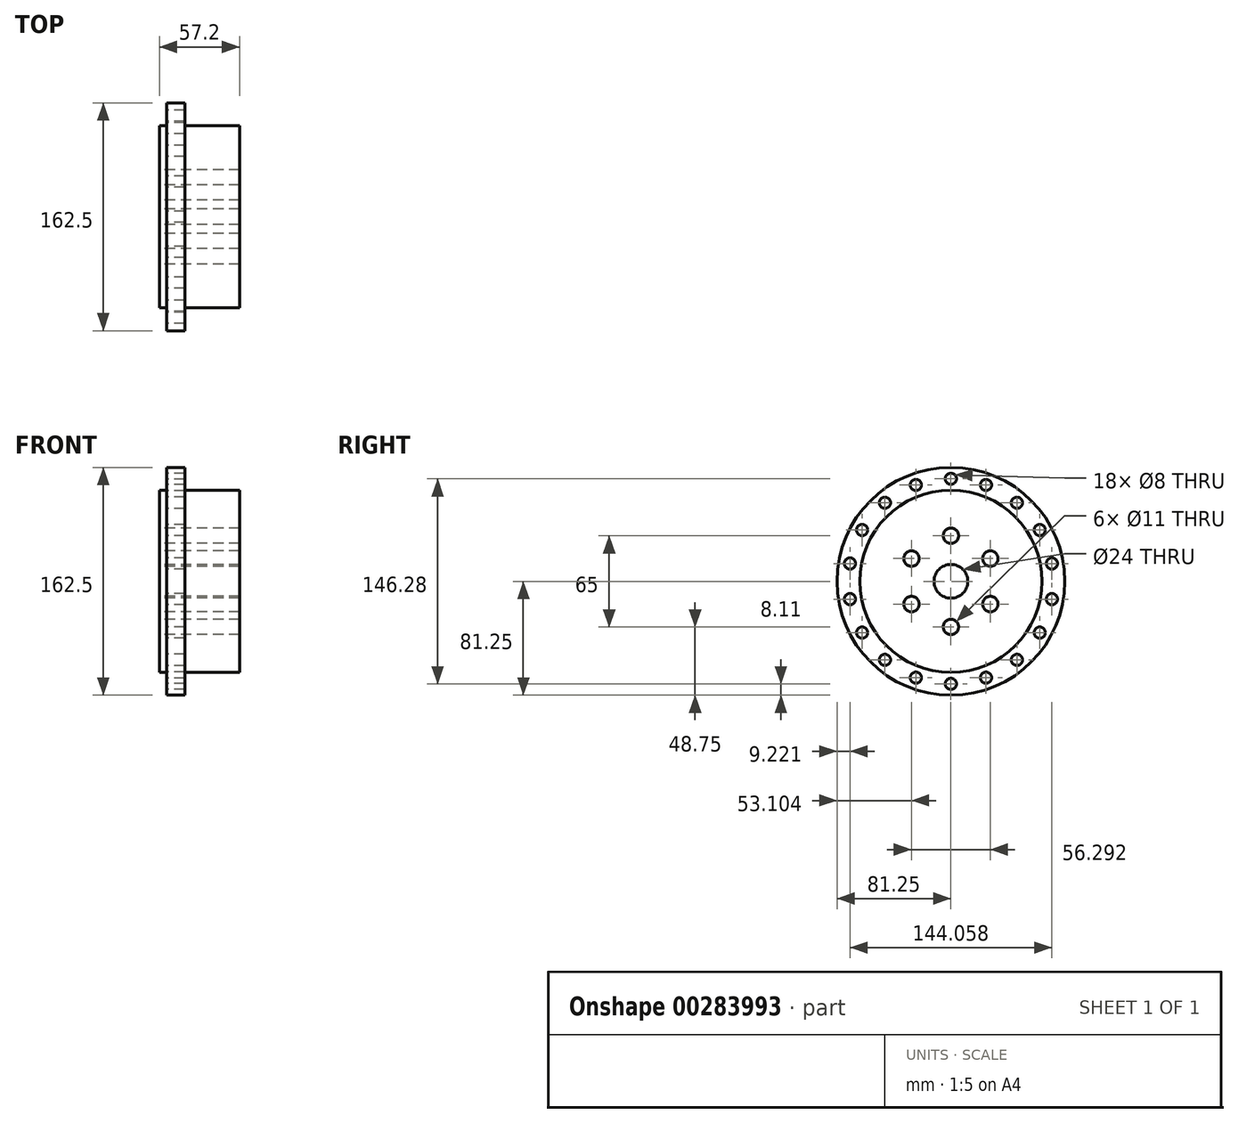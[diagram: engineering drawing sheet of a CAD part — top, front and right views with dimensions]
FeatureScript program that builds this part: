
annotation { "Feature Type Name" : "Feature", "Feature Type Description" : "" }
export const myFeature = defineFeature(function(context is Context, id is Id, definition is map)
    precondition{}
    {
        {
            var Q0;
            Q0=qCreatedBy(makeId("Right.planeOp"),FACE);
            var sketch = newSketch(context, id + "F0", { "sketchPlane" : qUnion([Q0])});
            skCircle(sketch, "E0", {"center": v(0, 0) * mm, "radius": 81.25 * mm});
            skCircle(sketch, "E1", {"center": v(0, 0) * mm, "radius": 65 * mm});
            skCircle(sketch, "E2", {"center": v(0, 0) * mm, "radius": 12 * mm});
            skCircle(sketch, "E3", {"center": v(0, 32.5) * mm, "radius": 5.5 * mm});
            skCircle(sketch, "E4.1.0", {"center": v(-28.15, 16.25) * mm, "radius": 5.5 * mm});
            skCircle(sketch, "E4.2.0", {"center": v(-28.15, -16.25) * mm, "radius": 5.5 * mm});
            skCircle(sketch, "E4.3.0", {"center": v(0, -32.5) * mm, "radius": 5.5 * mm});
            skCircle(sketch, "E4.4.0", {"center": v(28.15, -16.25) * mm, "radius": 5.5 * mm});
            skCircle(sketch, "E4.5.0", {"center": v(28.15, 16.25) * mm, "radius": 5.5 * mm});
            skCircle(sketch, "E5", {"center": v(0, 73.14) * mm, "radius": 4 * mm});
            skCircle(sketch, "E6.1.0", {"center": v(-25.02, 68.73) * mm, "radius": 4 * mm});
            skCircle(sketch, "E6.2.0", {"center": v(-47.01, 56.03) * mm, "radius": 4 * mm});
            skCircle(sketch, "E6.3.0", {"center": v(-63.34, 36.57) * mm, "radius": 4 * mm});
            skCircle(sketch, "E6.4.0", {"center": v(-72.03, 12.7) * mm, "radius": 4 * mm});
            skCircle(sketch, "E6.5.0", {"center": v(-72.03, -12.7) * mm, "radius": 4 * mm});
            skCircle(sketch, "E6.6.0", {"center": v(-63.34, -36.57) * mm, "radius": 4 * mm});
            skCircle(sketch, "E6.7.0", {"center": v(-47.01, -56.03) * mm, "radius": 4 * mm});
            skCircle(sketch, "E6.8.0", {"center": v(-25.02, -68.73) * mm, "radius": 4 * mm});
            skCircle(sketch, "E6.9.0", {"center": v(0, -73.14) * mm, "radius": 4 * mm});
            skCircle(sketch, "E6.10.0", {"center": v(25.02, -68.73) * mm, "radius": 4 * mm});
            skCircle(sketch, "E6.11.0", {"center": v(47.01, -56.03) * mm, "radius": 4 * mm});
            skCircle(sketch, "E6.12.0", {"center": v(63.34, -36.57) * mm, "radius": 4 * mm});
            skCircle(sketch, "E6.13.0", {"center": v(72.03, -12.7) * mm, "radius": 4 * mm});
            skCircle(sketch, "E6.14.0", {"center": v(72.03, 12.7) * mm, "radius": 4 * mm});
            skCircle(sketch, "E6.15.0", {"center": v(63.34, 36.57) * mm, "radius": 4 * mm});
            skCircle(sketch, "E6.16.0", {"center": v(47.01, 56.03) * mm, "radius": 4 * mm});
            skCircle(sketch, "E6.17.0", {"center": v(25.02, 68.73) * mm, "radius": 4 * mm});
            skSolve(sketch);
        }
        {
            var Q0;
            Q0=makeQuery(id+"F0.imprint","IMPRINT",FACE,{"disambiguationData":[TD([[makeQuery(id+"F0.imprint","IMPRINT",EDGE,{"derivedFrom":sQuery(id+"F0.wireOp",EDGE,"E1")}),1.0]])]});
            extrude(context, id + "F1", {"entities" : qUnion([Q0]), "depth" : 52 * mm});
        }
        {
            var Q0;
            Q0=makeQuery(id+"F0.imprint","IMPRINT",FACE,{"disambiguationData":[TD([[makeQuery(id+"F0.imprint","IMPRINT",EDGE,{"derivedFrom":sQuery(id+"F0.wireOp",EDGE,"E0")}),1.0]])]});
            extrude(context, id + "F2", {"entities" : qUnion([Q0]), "operationType" : NewBodyOperationType.ADD, "depth" : 52 / 4 * mm});
        }
        {
            var Q0;
            Q0=makeQuery(id+"F0.imprint","IMPRINT",FACE,{"disambiguationData":[TD([[makeQuery(id+"F0.imprint","IMPRINT",EDGE,{"derivedFrom":sQuery(id+"F0.wireOp",EDGE,"E1")}),1.0]])]});
            extrude(context, id + "F3", {"entities" : qUnion([Q0]), "operationType" : NewBodyOperationType.ADD, "oppositeDirection" : true, "depth" : 5.2 * mm});
        }
    });
